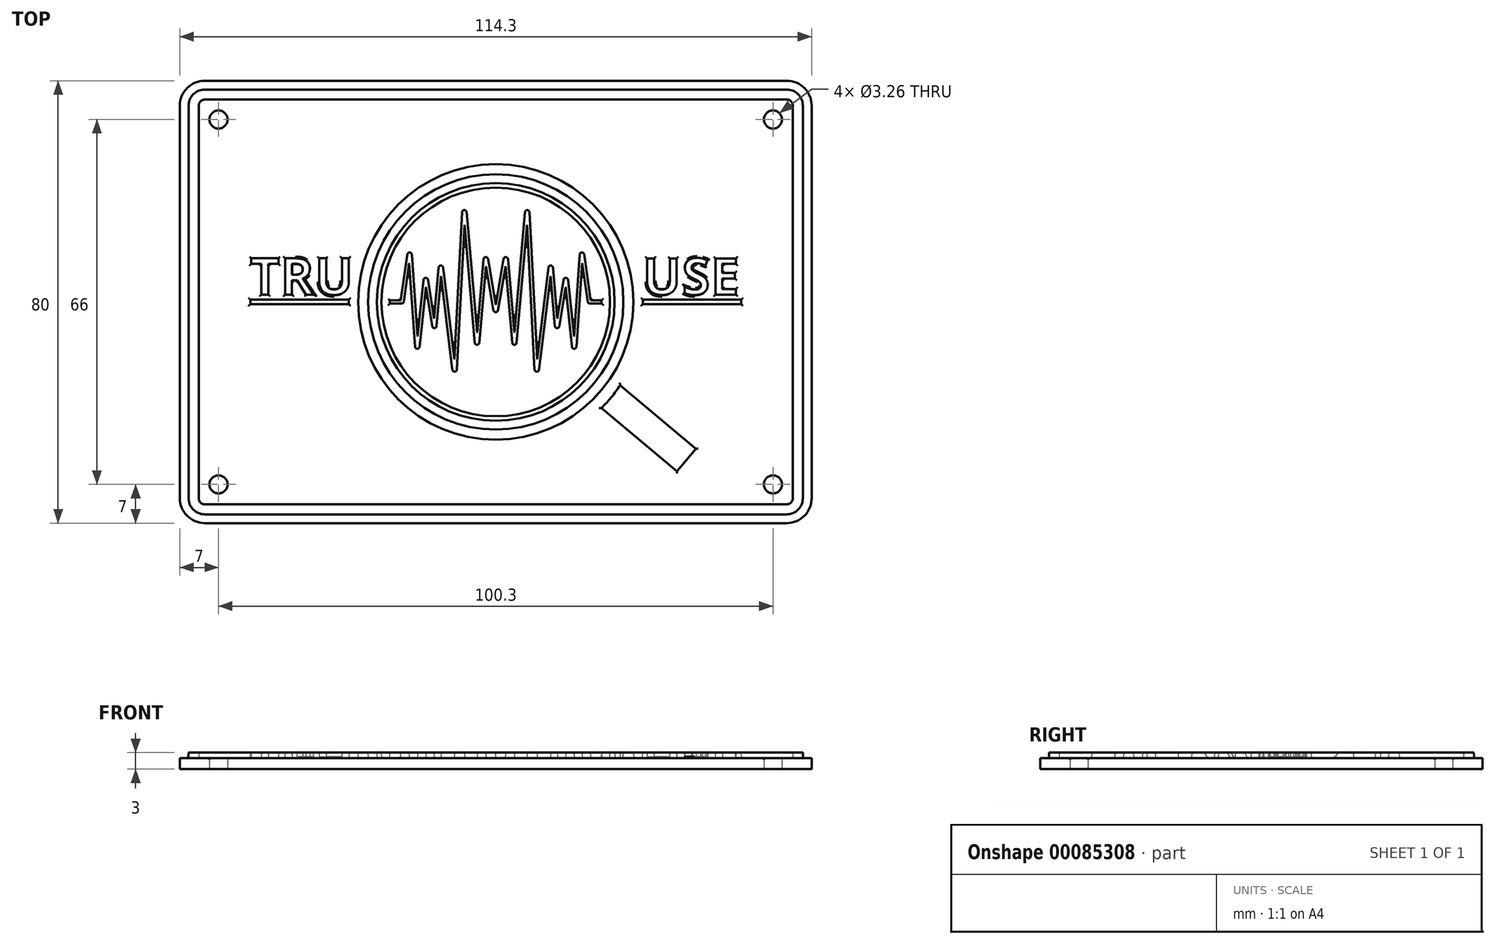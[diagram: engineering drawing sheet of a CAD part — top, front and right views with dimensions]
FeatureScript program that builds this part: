
annotation { "Feature Type Name" : "Feature", "Feature Type Description" : "" }
export const myFeature = defineFeature(function(context is Context, id is Id, definition is map)
    precondition{}
    {
        {
            var Q0;
            Q0=qCreatedBy(makeId("Front.planeOp"),FACE);
            var sketch = newSketch(context, id + "F0", { "sketchPlane" : qUnion([Q0])});
            skLineSegment(sketch, "E0.bottom", {"start": v(-57.15, 0) * mm, "end": v(57.15, 0) * mm});
            skLineSegment(sketch, "E0.top", {"start": v(-57.15, 2) * mm, "end": v(57.15, 2) * mm});
            skLineSegment(sketch, "E0.left", {"start": v(-57.15, 0) * mm, "end": v(-57.15, 2) * mm});
            skLineSegment(sketch, "E0.right", {"start": v(57.15, 0) * mm, "end": v(57.15, 2) * mm});
            skSolve(sketch);
        }
        {
            var Q0;
            Q0=makeQuery(id+"F0.imprint","IMPRINT",FACE,{"disambiguationData":[TD([[makeQuery(id+"F0.imprint","IMPRINT",EDGE,{"derivedFrom":sQuery(id+"F0.wireOp",EDGE,"E0.bottom")}),1.0]])]});
            extrude(context, id + "F1", {"entities" : qUnion([Q0]), "endBound" : BoundingType.SYMMETRIC, "depth" : 80 * mm});
        }
        {
            var Q0;
            Q0=qCreatedBy(makeId("Top.planeOp"),FACE);
            cPlane(context, id + "F2", {"entities" : qUnion([Q0]), "cplaneType" : CPlaneType.OFFSET, "offset" : 1.25 * mm, "width" : 150 * mm, "height" : 150 * mm});
        }
        {
            var Q0;
            Q0=qCreatedBy(id+"F2.planeOp",FACE);
            var sketch = newSketch(context, id + "F3", { "sketchPlane" : qUnion([Q0])});
            skCircle(sketch, "E1", {"center": v(0, 0) * mm, "radius": 25 * mm});
            skLineSegment(sketch, "E2.bottom", {"start": v(-44.5, -0.5) * mm, "end": v(-26.5, -0.5) * mm});
            skLineSegment(sketch, "E2.top", {"start": v(-44.5, 0.5) * mm, "end": v(-26.5, 0.5) * mm});
            skLineSegment(sketch, "E2.left", {"start": v(-44.5, -0.5) * mm, "end": v(-44.5, 0.5) * mm});
            skLineSegment(sketch, "E2.right", {"start": v(-26.5, -0.5) * mm, "end": v(-26.5, 0.5) * mm});
            skPoint(sketch, "E2.middle", {"position": v(-35.5, 0) * mm});
            skLineSegment(sketch, "E3.MirrorCS", {"start": v(44.5, 0.5) * mm, "end": v(26.5, 0.5) * mm});
            skLineSegment(sketch, "E4.MirrorCS", {"start": v(44.5, -0.5) * mm, "end": v(26.5, -0.5) * mm});
            skLineSegment(sketch, "E5.MirrorCS", {"start": v(26.5, -0.5) * mm, "end": v(26.5, 0.5) * mm});
            skLineSegment(sketch, "E6.MirrorCS", {"start": v(44.5, -0.5) * mm, "end": v(44.5, 0.5) * mm});
            skCircle(sketch, "E7", {"center": v(0, 0) * mm, "radius": 23 * mm});
            skSolve(sketch);
        }
        {
            var Q0;
            Q0=qSketchRegion(id+"F3",true);
            extrude(context, id + "F4", {"entities" : qUnion([Q0]), "operationType" : NewBodyOperationType.ADD, "depth" : 1.75 * mm, "hasDraft" : true, "draftAngle" : 3 * degree, "draftPullDirection" : true});
        }
        {
            var Q0;
            Q0=qCreatedBy(id+"F2.planeOp",FACE);
            var sketch = newSketch(context, id + "F5", { "sketchPlane" : qUnion([Q0])});
            skCircle(sketch, "E8", {"center": v(0, 0) * mm, "radius": 21.6 * mm});
            skCircle(sketch, "E9", {"center": v(0, 0) * mm, "radius": 20.6 * mm});
            skSolve(sketch);
        }
        {
            var Q0;
            Q0=qSketchRegion(id+"F5",true);
            extrude(context, id + "F6", {"entities" : qUnion([Q0]), "operationType" : NewBodyOperationType.ADD, "depth" : 1.75 * mm, "hasDraft" : true, "draftAngle" : 3 * degree, "draftPullDirection" : true});
        }
        {
            var Q0;
            Q0=qCreatedBy(id+"F2.planeOp",FACE);
            var sketch = newSketch(context, id + "F7", { "sketchPlane" : qUnion([Q0])});
            skLineSegment(sketch, "E10.0", {"start": v(19, -19.19) * mm, "end": v(32.78, -30.76) * mm});
            skLineSegment(sketch, "E11.0", {"start": v(22.49, -14.94) * mm, "end": v(36.32, -26.55) * mm});
            skLineSegment(sketch, "E12", {"start": v(36.32, -26.55) * mm, "end": v(32.78, -30.76) * mm});
            skArc(sketch, "E13", {"start": v(19, -19.19) * mm, "mid": v(20.85, -17.15) * mm, "end": v(22.49, -14.94) * mm});
            skSolve(sketch);
        }
        {
            var Q0;
            Q0=qSketchRegion(id+"F7",true);
            extrude(context, id + "F8", {"entities" : qUnion([Q0]), "operationType" : NewBodyOperationType.ADD, "depth" : 1.75 * mm, "hasDraft" : true, "draftAngle" : 3 * degree, "draftPullDirection" : true});
        }
        {
            var Q0;
            Q0=qCreatedBy(id+"F2.planeOp",FACE);
            var sketch = newSketch(context, id + "F9", { "sketchPlane" : qUnion([Q0])});
            skText(sketch, "E14", { "text": "TRU", "fontName": "OpenSans-Bold.ttf"});
            skText(sketch, "E15", { "text": "USE", "fontName": "OpenSans-Bold.ttf"});
            const initialGuessF9  = {"E14": [-0.0445, 0.00125, 1, 0, 0.00679], "E15": [0.0265, 0.00125, 1, 0, 0.00678]};
            skSetInitialGuess(sketch, initialGuessF9);
            skSolve(sketch);
        }
        {
            var Q0;
            Q0=qSketchRegion(id+"F9",true);
            extrude(context, id + "F10", {"entities" : qUnion([Q0]), "operationType" : NewBodyOperationType.ADD, "depth" : 1.75 * mm, "hasDraft" : true, "draftAngle" : 3 * degree, "draftPullDirection" : true});
        }
        {
            var Q0;
            Q0=qCreatedBy(id+"F2.planeOp",FACE);
            var sketch = newSketch(context, id + "F11", { "sketchPlane" : qUnion([Q0])});
            skPoint(sketch, "E16.middle", {"position": v(0, 0) * mm});
            skLineSegment(sketch, "E17.bottom", {"start": v(52.65, 38.5) * mm, "end": v(-52.65, 38.5) * mm});
            skLineSegment(sketch, "E17.top", {"start": v(52.65, -38.5) * mm, "end": v(-52.65, -38.5) * mm});
            skLineSegment(sketch, "E17.left", {"start": v(55.65, 35.5) * mm, "end": v(55.65, -35.5) * mm});
            skLineSegment(sketch, "E17.right", {"start": v(-55.65, 35.5) * mm, "end": v(-55.65, -35.5) * mm});
            skLineSegment(sketch, "E18.bottom", {"start": v(52.65, 36.5) * mm, "end": v(-52.65, 36.5) * mm});
            skLineSegment(sketch, "E18.top", {"start": v(52.65, -36.5) * mm, "end": v(-52.65, -36.5) * mm});
            skLineSegment(sketch, "E18.left", {"start": v(53.65, 35.5) * mm, "end": v(53.65, -35.5) * mm});
            skLineSegment(sketch, "E18.right", {"start": v(-53.65, 35.5) * mm, "end": v(-53.65, -35.5) * mm});
            skPoint(sketch, "E19.visualSharp", {"position": v(-55.65, 38.5) * mm});
            skArc(sketch, "E19.filletArc", {"start": v(-52.65, 38.5) * mm, "mid": v(-54.77, 37.62) * mm, "end": v(-55.65, 35.5) * mm});
            skPoint(sketch, "E20.visualSharp", {"position": v(55.65, 38.5) * mm});
            skArc(sketch, "E20.filletArc", {"start": v(55.65, 35.5) * mm, "mid": v(54.77, 37.62) * mm, "end": v(52.65, 38.5) * mm});
            skPoint(sketch, "E21.visualSharp", {"position": v(55.65, -38.5) * mm});
            skArc(sketch, "E21.filletArc", {"start": v(52.65, -38.5) * mm, "mid": v(54.77, -37.62) * mm, "end": v(55.65, -35.5) * mm});
            skPoint(sketch, "E22.visualSharp", {"position": v(-55.65, -38.5) * mm});
            skArc(sketch, "E22.filletArc", {"start": v(-55.65, -35.5) * mm, "mid": v(-54.77, -37.62) * mm, "end": v(-52.65, -38.5) * mm});
            skPoint(sketch, "E23.visualSharp", {"position": v(53.65, 36.5) * mm});
            skArc(sketch, "E23.filletArc", {"start": v(53.65, 35.5) * mm, "mid": v(53.36, 36.2) * mm, "end": v(52.65, 36.5) * mm});
            skPoint(sketch, "E24.visualSharp", {"position": v(-53.65, 36.5) * mm});
            skArc(sketch, "E24.filletArc", {"start": v(-52.65, 36.5) * mm, "mid": v(-53.36, 36.2) * mm, "end": v(-53.65, 35.5) * mm});
            skPoint(sketch, "E25.visualSharp", {"position": v(-53.65, -36.5) * mm});
            skArc(sketch, "E25.filletArc", {"start": v(-53.65, -35.5) * mm, "mid": v(-53.36, -36.2) * mm, "end": v(-52.65, -36.5) * mm});
            skPoint(sketch, "E26.visualSharp", {"position": v(53.65, -36.5) * mm});
            skArc(sketch, "E26.filletArc", {"start": v(52.65, -36.5) * mm, "mid": v(53.36, -36.2) * mm, "end": v(53.65, -35.5) * mm});
            skSolve(sketch);
        }
        {
            var Q0;
            Q0=qSketchRegion(id+"F11",true);
            extrude(context, id + "F12", {"entities" : qUnion([Q0]), "operationType" : NewBodyOperationType.ADD, "depth" : 1.75 * mm, "hasDraft" : true, "draftAngle" : 3 * degree, "draftPullDirection" : true});
        }
        {
            var Q0;
            Q0=qCreatedBy(id+"F2.planeOp",FACE);
            var sketch = newSketch(context, id + "F13", { "sketchPlane" : qUnion([Q0])});
            skLineSegment(sketch, "E27.bottom", {"start": v(-17.03, -0.38) * mm, "end": v(-19.25, -0.37) * mm});
            skLineSegment(sketch, "E27.top", {"start": v(-17.25, 0.38) * mm, "end": v(-19.25, 0.38) * mm});
            skLineSegment(sketch, "E27.right", {"start": v(-19.25, -0.37) * mm, "end": v(-19.25, 0.38) * mm});
            skPoint(sketch, "E27.middle", {"position": v(-18.25, 0) * mm});
            skLineSegment(sketch, "E28", {"start": v(-17.25, 0.37) * mm, "end": v(-16.09, 8.62) * mm});
            skLineSegment(sketch, "E29.0", {"start": v(-16.53, 0.06) * mm, "end": v(-15.68, 6.16) * mm});
            skPoint(sketch, "E27.left.start.orphan", {"position": v(-17.25, -0.38) * mm});
            skPoint(sketch, "E30.visualSharp", {"position": v(-16.6, -0.38) * mm});
            skArc(sketch, "E30.filletArc", {"start": v(-17.03, -0.38) * mm, "mid": v(-16.7, -0.25) * mm, "end": v(-16.53, 0.06) * mm});
            skLineSegment(sketch, "E31", {"start": v(-15.68, 6.16) * mm, "end": v(-14.68, -8.1) * mm});
            skLineSegment(sketch, "E32.0", {"start": v(-15.1, 8.58) * mm, "end": v(-14.13, -5.19) * mm});
            skPoint(sketch, "E33.visualSharp", {"position": v(-15.43, 13.33) * mm});
            skArc(sketch, "E33.filletArc", {"start": v(-15.1, 8.58) * mm, "mid": v(-15.58, 9.05) * mm, "end": v(-16.09, 8.62) * mm});
            skLineSegment(sketch, "E34", {"start": v(-14.13, -5.19) * mm, "end": v(-13.16, 4) * mm});
            skLineSegment(sketch, "E35.0", {"start": v(-13.68, -8.1) * mm, "end": v(-12.62, 2.03) * mm});
            skLineSegment(sketch, "E36", {"start": v(-12.62, 2.03) * mm, "end": v(-11.6, -4.4) * mm});
            skLineSegment(sketch, "E37.0", {"start": v(-12.17, 4.02) * mm, "end": v(-11.18, -2.27) * mm});
            skLineSegment(sketch, "E38", {"start": v(-11.18, -2.27) * mm, "end": v(-10.43, 6.22) * mm});
            skLineSegment(sketch, "E39.0", {"start": v(-10.6, -4.37) * mm, "end": v(-9.9, 3.78) * mm});
            skLineSegment(sketch, "E40", {"start": v(-9.9, 3.78) * mm, "end": v(-7.92, -12.26) * mm});
            skLineSegment(sketch, "E41.0", {"start": v(-9.44, 6.24) * mm, "end": v(-7.53, -9.33) * mm});
            skLineSegment(sketch, "E42", {"start": v(-7.53, -9.33) * mm, "end": v(-6.19, 16.22) * mm});
            skLineSegment(sketch, "E43.0", {"start": v(-6.93, -12.22) * mm, "end": v(-5.63, 12.61) * mm});
            skLineSegment(sketch, "E44", {"start": v(-5.63, 12.61) * mm, "end": v(-3.88, -7.38) * mm});
            skLineSegment(sketch, "E45.0", {"start": v(-5.2, 16.24) * mm, "end": v(-3.38, -4.47) * mm});
            skLineSegment(sketch, "E46", {"start": v(-3.38, -4.47) * mm, "end": v(-2.31, 7.74) * mm});
            skLineSegment(sketch, "E47.0", {"start": v(-2.88, -7.38) * mm, "end": v(-1.73, 5.74) * mm});
            skLineSegment(sketch, "E48", {"start": v(0, 12.7) * mm, "end": v(0, -16.33) * mm, "construction": true});
            skLineSegment(sketch, "E49", {"start": v(-1.73, 5.74) * mm, "end": v(-0.5, -1.53) * mm});
            skLineSegment(sketch, "E50.0", {"start": v(-1.32, 7.78) * mm, "end": v(0, 0.04) * mm});
            skPoint(sketch, "E51.visualSharp", {"position": v(-14.28, -13.8) * mm});
            skArc(sketch, "E51.filletArc", {"start": v(-14.68, -8.1) * mm, "mid": v(-14.19, -8.56) * mm, "end": v(-13.68, -8.1) * mm});
            skPoint(sketch, "E52.visualSharp", {"position": v(-12.77, 7.78) * mm});
            skArc(sketch, "E52.filletArc", {"start": v(-12.17, 4.02) * mm, "mid": v(-12.68, 4.45) * mm, "end": v(-13.16, 4) * mm});
            skPoint(sketch, "E53.visualSharp", {"position": v(-10.96, -8.42) * mm});
            skArc(sketch, "E53.filletArc", {"start": v(-11.6, -4.4) * mm, "mid": v(-11.09, -4.82) * mm, "end": v(-10.6, -4.37) * mm});
            skPoint(sketch, "E54.visualSharp", {"position": v(-10.02, 10.96) * mm});
            skArc(sketch, "E54.filletArc", {"start": v(-9.44, 6.24) * mm, "mid": v(-9.94, 6.67) * mm, "end": v(-10.43, 6.22) * mm});
            skPoint(sketch, "E55.visualSharp", {"position": v(-7.23, -17.93) * mm});
            skArc(sketch, "E55.filletArc", {"start": v(-7.92, -12.26) * mm, "mid": v(-7.4, -12.7) * mm, "end": v(-6.93, -12.22) * mm});
            skPoint(sketch, "E56.visualSharp", {"position": v(-5.81, 23.36) * mm});
            skArc(sketch, "E56.filletArc", {"start": v(-5.2, 16.24) * mm, "mid": v(-5.7, 16.7) * mm, "end": v(-6.19, 16.22) * mm});
            skPoint(sketch, "E57.visualSharp", {"position": v(-3.38, -13.07) * mm});
            skArc(sketch, "E57.filletArc", {"start": v(-3.88, -7.38) * mm, "mid": v(-3.38, -7.84) * mm, "end": v(-2.88, -7.38) * mm});
            skPoint(sketch, "E58.visualSharp", {"position": v(-1.97, 11.61) * mm});
            skArc(sketch, "E58.filletArc", {"start": v(-1.32, 7.78) * mm, "mid": v(-1.83, 8.2) * mm, "end": v(-2.31, 7.74) * mm});
            skArc(sketch, "E59.MirrorCS", {"start": v(17.03, -0.38) * mm, "mid": v(16.7, -0.25) * mm, "end": v(16.53, 0.06) * mm});
            skArc(sketch, "E60.MirrorCS", {"start": v(5.2, 16.24) * mm, "mid": v(5.7, 16.7) * mm, "end": v(6.19, 16.22) * mm});
            skArc(sketch, "E61.MirrorCS", {"start": v(1.32, 7.78) * mm, "mid": v(1.83, 8.2) * mm, "end": v(2.31, 7.74) * mm});
            skArc(sketch, "E62.MirrorCS", {"start": v(3.88, -7.38) * mm, "mid": v(3.38, -7.84) * mm, "end": v(2.88, -7.38) * mm});
            skArc(sketch, "E63.MirrorCS", {"start": v(14.68, -8.1) * mm, "mid": v(14.19, -8.56) * mm, "end": v(13.68, -8.1) * mm});
            skArc(sketch, "E64.MirrorCS", {"start": v(11.6, -4.4) * mm, "mid": v(11.09, -4.82) * mm, "end": v(10.6, -4.37) * mm});
            skArc(sketch, "E65.MirrorCS", {"start": v(9.44, 6.24) * mm, "mid": v(9.94, 6.67) * mm, "end": v(10.43, 6.22) * mm});
            skArc(sketch, "E66.MirrorCS", {"start": v(15.1, 8.58) * mm, "mid": v(15.58, 9.05) * mm, "end": v(16.09, 8.62) * mm});
            skArc(sketch, "E67.MirrorCS", {"start": v(12.17, 4.02) * mm, "mid": v(12.68, 4.45) * mm, "end": v(13.16, 4) * mm});
            skArc(sketch, "E68.MirrorCS", {"start": v(7.92, -12.26) * mm, "mid": v(7.4, -12.7) * mm, "end": v(6.93, -12.22) * mm});
            skLineSegment(sketch, "E69.MirrorCS", {"start": v(19.25, -0.37) * mm, "end": v(19.25, 0.38) * mm});
            skLineSegment(sketch, "E70.MirrorCS", {"start": v(17.03, -0.38) * mm, "end": v(19.25, -0.37) * mm});
            skPoint(sketch, "E71.MirrorP", {"position": v(16.6, -0.38) * mm});
            skLineSegment(sketch, "E72.MirrorCS", {"start": v(17.25, 0.38) * mm, "end": v(19.25, 0.38) * mm});
            skPoint(sketch, "E73.MirrorP", {"position": v(17.25, -0.38) * mm});
            skPoint(sketch, "E74.MirrorP", {"position": v(18.25, 0) * mm});
            skLineSegment(sketch, "E75.MirrorCS", {"start": v(7.53, -9.33) * mm, "end": v(6.19, 16.22) * mm});
            skPoint(sketch, "E76.MirrorP", {"position": v(12.77, 7.78) * mm});
            skLineSegment(sketch, "E77.MirrorCS", {"start": v(3.38, -4.47) * mm, "end": v(2.31, 7.74) * mm});
            skLineSegment(sketch, "E78.MirrorCS", {"start": v(12.17, 4.02) * mm, "end": v(11.18, -2.27) * mm});
            skLineSegment(sketch, "E79.MirrorCS", {"start": v(1.73, 5.74) * mm, "end": v(0.5, -1.53) * mm});
            skPoint(sketch, "E80.MirrorP", {"position": v(14.28, -13.8) * mm});
            skLineSegment(sketch, "E81.MirrorCS", {"start": v(1.32, 7.78) * mm, "end": v(0, 0.04) * mm});
            skLineSegment(sketch, "E82.MirrorCS", {"start": v(10.6, -4.37) * mm, "end": v(9.9, 3.78) * mm});
            skLineSegment(sketch, "E83.MirrorCS", {"start": v(9.9, 3.78) * mm, "end": v(7.92, -12.26) * mm});
            skPoint(sketch, "E84.MirrorP", {"position": v(10.96, -8.42) * mm});
            skLineSegment(sketch, "E85.MirrorCS", {"start": v(9.44, 6.24) * mm, "end": v(7.53, -9.33) * mm});
            skLineSegment(sketch, "E86.MirrorCS", {"start": v(2.88, -7.38) * mm, "end": v(1.73, 5.74) * mm});
            skLineSegment(sketch, "E87.MirrorCS", {"start": v(12.62, 2.03) * mm, "end": v(11.6, -4.4) * mm});
            skPoint(sketch, "E88.MirrorP", {"position": v(1.97, 11.61) * mm});
            skPoint(sketch, "E89.MirrorP", {"position": v(3.38, -13.07) * mm});
            skPoint(sketch, "E90.MirrorP", {"position": v(15.43, 13.33) * mm});
            skPoint(sketch, "E91.MirrorP", {"position": v(10.02, 10.96) * mm});
            skLineSegment(sketch, "E92.MirrorCS", {"start": v(5.2, 16.24) * mm, "end": v(3.38, -4.47) * mm});
            skLineSegment(sketch, "E93.MirrorCS", {"start": v(17.25, 0.37) * mm, "end": v(16.09, 8.62) * mm});
            skLineSegment(sketch, "E94.MirrorCS", {"start": v(5.63, 12.61) * mm, "end": v(3.88, -7.38) * mm});
            skLineSegment(sketch, "E95.MirrorCS", {"start": v(14.13, -5.19) * mm, "end": v(13.16, 4) * mm});
            skLineSegment(sketch, "E96.MirrorCS", {"start": v(13.68, -8.1) * mm, "end": v(12.62, 2.03) * mm});
            skLineSegment(sketch, "E97.MirrorCS", {"start": v(15.68, 6.16) * mm, "end": v(14.68, -8.1) * mm});
            skLineSegment(sketch, "E98.MirrorCS", {"start": v(6.93, -12.22) * mm, "end": v(5.63, 12.61) * mm});
            skLineSegment(sketch, "E99.MirrorCS", {"start": v(15.1, 8.58) * mm, "end": v(14.13, -5.19) * mm});
            skLineSegment(sketch, "E100.MirrorCS", {"start": v(16.53, 0.06) * mm, "end": v(15.68, 6.16) * mm});
            skLineSegment(sketch, "E101.MirrorCS", {"start": v(11.18, -2.27) * mm, "end": v(10.43, 6.22) * mm});
            skPoint(sketch, "E102.visualSharp", {"position": v(0, -4.42) * mm});
            skArc(sketch, "E102.filletArc", {"start": v(-0.5, -1.53) * mm, "mid": v(0, -1.95) * mm, "end": v(0.5, -1.53) * mm});
            skSolve(sketch);
        }
        {
            var Q0;
            Q0=qSketchRegion(id+"F13",true);
            extrude(context, id + "F14", {"entities" : qUnion([Q0]), "operationType" : NewBodyOperationType.ADD, "depth" : 1.75 * mm, "hasDraft" : true, "draftAngle" : 3 * degree, "draftPullDirection" : true});
        }
        {
            var Q0;
            Q0=makeQuery(id+"F1.opExtrude","CAP_EDGE",EDGE,{"disambiguationData":[OSD([sQuery(id+"F0.wireOp",EDGE,"E0.right")])],"isStart":true});
            var Q1;
            Q1=makeQuery(id+"F1.opExtrude","CAP_EDGE",EDGE,{"disambiguationData":[OSD([sQuery(id+"F0.wireOp",EDGE,"E0.right")])],"isStart":false});
            var Q2;
            Q2=makeQuery(id+"F1.opExtrude","CAP_EDGE",EDGE,{"disambiguationData":[OSD([sQuery(id+"F0.wireOp",EDGE,"E0.left")])],"isStart":false});
            var Q3;
            Q3=makeQuery(id+"F1.opExtrude","CAP_EDGE",EDGE,{"disambiguationData":[OSD([sQuery(id+"F0.wireOp",EDGE,"E0.left")])],"isStart":true});
            fillet(context, id + "F15", {"entities" : qUnion([Q0, Q1, Q2, Q3]), "radius" : 4.5 * mm, "tangentPropagation" : true, "allowEdgeOverflow" : false});
        }
        {
            var Q0;
            Q0=qCreatedBy(makeId("Top.planeOp"),FACE);
            var sketch = newSketch(context, id + "F16", { "sketchPlane" : qUnion([Q0])});
            skCircle(sketch, "E103", {"center": v(-50.15, 33) * mm, "radius": 1.63 * mm});
            skCircle(sketch, "E104.MirrorC", {"center": v(50.15, 33) * mm, "radius": 1.63 * mm});
            skCircle(sketch, "E105.MirrorC", {"center": v(-50.15, -33) * mm, "radius": 1.63 * mm});
            skCircle(sketch, "E106.MirrorC", {"center": v(50.15, -33) * mm, "radius": 1.63 * mm});
            skSolve(sketch);
        }
        {
            var Q0;
            Q0=qSketchRegion(id+"F16",true);
            extrude(context, id + "F17", {"entities" : qUnion([Q0]), "operationType" : NewBodyOperationType.REMOVE, "endBound" : BoundingType.THROUGH_ALL, "depth" : 25 * mm});
        }
        {
            var Q0;
            {var subQ87=makeQuery(id+"F4.opExtrude","SWEPT_FACE",FACE,{"disambiguationData":[OSD([sQuery(id+"F3.wireOp",EDGE,"E1")])]});var subQ104=sQuery(id+"F0.wireOp",EDGE,"E0.left");var subQ105=sQuery(id+"F0.wireOp",EDGE,"E0.top");var subQ110=makeQuery(id+"F1.opExtrude","SWEPT_FACE",FACE,{"disambiguationData":[OSD([subQ104])]});Q0=makeQuery(id+"F12.boolean.opBoolean","SPLIT",FACE,{"disambiguationData":[TD([subQ87])],"derivedFrom":makeQuery(id+"F10.boolean.opBoolean","SPLIT",FACE,{"disambiguationData":[TD([subQ110])],"derivedFrom":makeQuery(id+"F4.boolean.opBoolean","SPLIT",FACE,{"disambiguationData":[TD([subQ110])],"derivedFrom":makeQuery(id+"F1.opExtrude","SWEPT_FACE",FACE,{"disambiguationData":[OSD([subQ105])]})})})});}
            var Q1;
            {var subQ0=makeQuery(id+"F4.opExtrude","SWEPT_FACE",FACE,{"disambiguationData":[OSD([sQuery(id+"F3.wireOp",EDGE,"E7")])]});Q1=makeQuery(id+"F6.boolean.opBoolean","SPLIT",FACE,{"disambiguationData":[TD([subQ0])],"derivedFrom":makeQuery(id+"F4.boolean.opBoolean","SPLIT",FACE,{"disambiguationData":[TD([subQ0])],"derivedFrom":makeQuery(id+"F1.opExtrude","SWEPT_FACE",FACE,{"disambiguationData":[OSD([sQuery(id+"F0.wireOp",EDGE,"E0.top")])]})})});}
            var Q2;
            Q2=makeQuery(id+"F6.boolean.opBoolean","SPLIT",FACE,{"disambiguationData":[TD([makeQuery(id+"F6.opExtrude","SWEPT_FACE",FACE,{"disambiguationData":[OSD([sQuery(id+"F5.wireOp",EDGE,"E9")])]})])],"derivedFrom":makeQuery(id+"F4.boolean.opBoolean","SPLIT",FACE,{"disambiguationData":[TD([makeQuery(id+"F4.opExtrude","SWEPT_FACE",FACE,{"disambiguationData":[OSD([sQuery(id+"F3.wireOp",EDGE,"E7")])]})])],"derivedFrom":makeQuery(id+"F1.opExtrude","SWEPT_FACE",FACE,{"disambiguationData":[OSD([sQuery(id+"F0.wireOp",EDGE,"E0.top")])]})})});
            var Q3;
            {var subQ4=sQuery(id+"F0.wireOp",EDGE,"E0.left");var subQ5=sQuery(id+"F0.wireOp",EDGE,"E0.top");var subQ16=makeQuery(id+"F1.opExtrude","SWEPT_FACE",FACE,{"disambiguationData":[OSD([subQ4])]});Q3=makeQuery(id+"F12.boolean.opBoolean","INTERSECT",EDGE,{"derivedFrom":[makeQuery(id+"F10.boolean.opBoolean","SPLIT",FACE,{"disambiguationData":[TD([subQ16])],"derivedFrom":makeQuery(id+"F4.boolean.opBoolean","SPLIT",FACE,{"disambiguationData":[TD([subQ16])],"derivedFrom":makeQuery(id+"F1.opExtrude","SWEPT_FACE",FACE,{"disambiguationData":[OSD([subQ5])]})})}),makeQuery(id+"F12.opExtrude","SWEPT_FACE",FACE,{"disambiguationData":[OSD([sQuery(id+"F11.wireOp",EDGE,"E17.top")])]})]});}
            fillet(context, id + "F18", {"entities" : qUnion([Q0, Q1, Q2, Q3]), "radius" : .25 * mm, "tangentPropagation" : true, "allowEdgeOverflow" : false});
        }
    });
